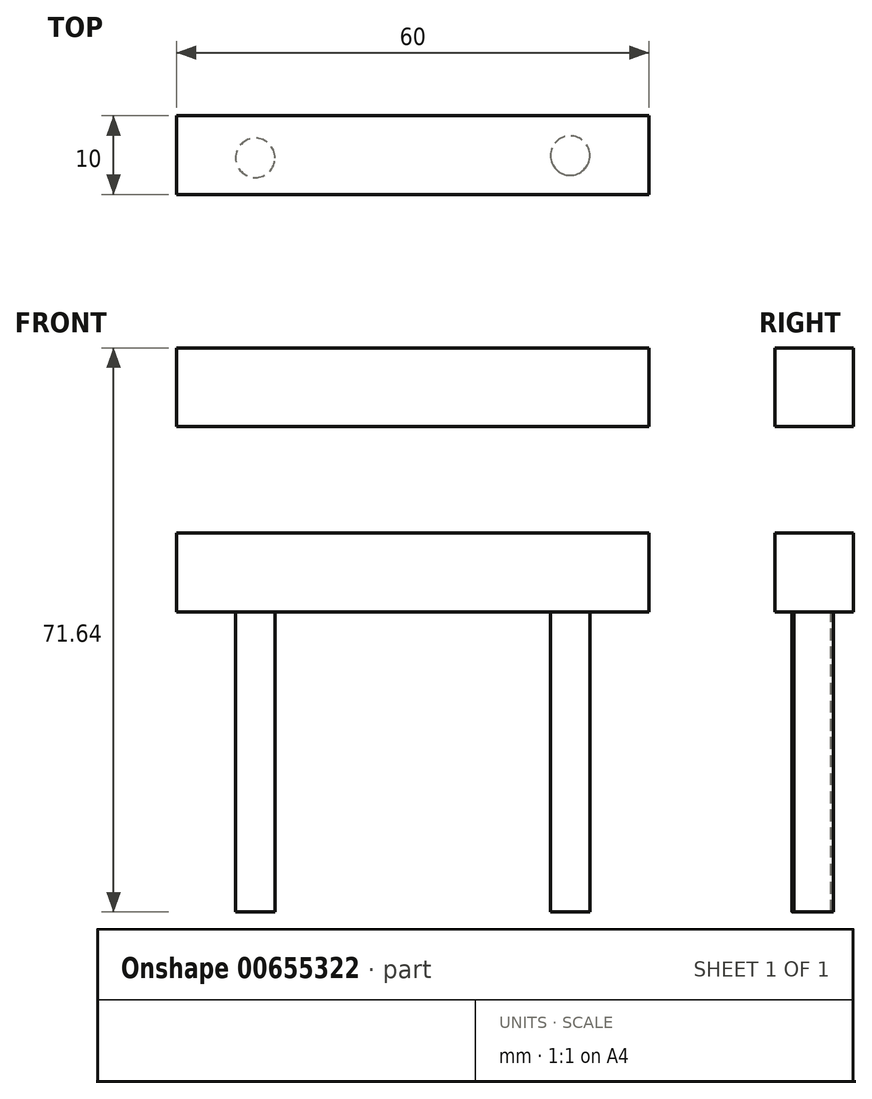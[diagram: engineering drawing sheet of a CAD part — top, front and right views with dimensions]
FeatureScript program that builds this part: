
annotation { "Feature Type Name" : "Feature", "Feature Type Description" : "" }
export const myFeature = defineFeature(function(context is Context, id is Id, definition is map)
    precondition{}
    {
        {
            var Q0;
            Q0=qCreatedBy(makeId("Front.planeOp"),FACE);
            var sketch = newSketch(context, id + "F0", { "sketchPlane" : qUnion([Q0])});
            skLineSegment(sketch, "E0.bottom", {"start": v(0, 0) * mm, "end": v(60, 0) * mm});
            skLineSegment(sketch, "E0.top", {"start": v(0, 10) * mm, "end": v(60, 10) * mm});
            skLineSegment(sketch, "E0.left", {"start": v(0, 0) * mm, "end": v(0, 10) * mm});
            skLineSegment(sketch, "E0.right", {"start": v(60, 0) * mm, "end": v(60, 10) * mm});
            skLineSegment(sketch, "E1.bottom", {"start": v(0, -13.54) * mm, "end": v(60, -13.54) * mm});
            skLineSegment(sketch, "E1.top", {"start": v(0, -23.54) * mm, "end": v(60, -23.54) * mm});
            skLineSegment(sketch, "E1.left", {"start": v(0, -13.54) * mm, "end": v(0, -23.54) * mm});
            skLineSegment(sketch, "E1.right", {"start": v(60, -13.54) * mm, "end": v(60, -23.54) * mm});
            skSolve(sketch);
        }
        {
            var Q0;
            Q0=makeQuery(id+"F0.imprint","IMPRINT",FACE,{"disambiguationData":[TD([[makeQuery(id+"F0.imprint","IMPRINT",EDGE,{"derivedFrom":sQuery(id+"F0.wireOp",EDGE,"E0.bottom")}),1.0]])]});
            var Q1;
            Q1=makeQuery(id+"F0.imprint","IMPRINT",FACE,{"disambiguationData":[TD([[makeQuery(id+"F0.imprint","IMPRINT",EDGE,{"derivedFrom":sQuery(id+"F0.wireOp",EDGE,"E1.bottom")}),-1.0]])]});
            extrude(context, id + "F1", {"entities" : qUnion([Q0, Q1]), "depth" : 10 * mm, "offsetDistance" : 25.4 * mm});
        }
        {
            var Q0;
            Q0=makeQuery(id+"F1.opExtrude","SWEPT_FACE",FACE,{"disambiguationData":[OSD([sQuery(id+"F0.wireOp",EDGE,"E1.top")])]});
            var sketch = newSketch(context, id + "F2", { "sketchPlane" : qUnion([Q0])});
            skCircle(sketch, "E2", {"center": v(10, 5.36) * mm, "radius": 2.5 * mm});
            skCircle(sketch, "E3", {"center": v(50, 5.07) * mm, "radius": 2.5 * mm});
            skSolve(sketch);
        }
        {
            var Q0;
            Q0 = qSketchRegion(id + "F2", true);
            extrude(context, id + "F3", {"entities" : qUnion([Q0]), "operationType" : NewBodyOperationType.ADD, "depth" : 38.1 * mm, "offsetDistance" : 25.4 * mm});
        }
    });
